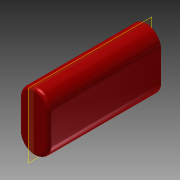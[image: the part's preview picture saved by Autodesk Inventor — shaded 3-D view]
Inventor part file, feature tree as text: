
AUTODESK INVENTOR PART (.ipt)
format: ipt  version: 2013 (Build 170138000, 138)  size: 93,696 bytes
history: native  units: mm (DEFAULTED — no unit token found)
features: plane x2, extrude x1, fillet x1, sketch x1, reference x1
ambient origin geometry x8: Origin, YZ Plane, XZ Plane, XY Plane, X Axis, Y Axis, Z Axis, Center Point
bodies: Solid1 (feature_tree)
feature tree (6):
  extrude  "Extrusion1"  Depth=0.381mm
  fillet  "Fillet1"  [1 undecoded]
  plane  "Work Plane1"
  plane  "Work Plane2"
  sketch  "Sketch1"  dims[d0=12.7mm d1=0.0mm d2=0.381mm]
  reference  "Reference1"
note: 1 required parameter value undecoded (feature->parameter linkage not recoverable at this tier; creation-order binding heuristic only, values carry confidence <= 0.55)
